# Revit family: Drain_Floor_15-Inch-Round_Zurn-Z1737_Extra-Heavy-Duty
name_source: partatom
category: Plumbing Fixtures
units: mm (PartAtom-declared; Revit-internal decimal feet)

## family parameters
Always vertical = Yes
Cut with Voids When Loaded = No
Maintain Annotation Orientation = No
OmniClass Number = 23.45.55.21
OmniClass Title = Drains (Wastes)
Part Type = Normal
Room Calculation Point = No
Round Connector Dimension = Use Radius
Shared = No
Work Plane-Based = No

## types (2) — shared parameters
Approx. Weight (Lbs) = 85 "
Assembly Code = D2030300
Body HT Dim 'E' = 5.5 "
CW Connection = No
Default Elevation = 10 "
Description = 15 INCH DIAMETER FLOOR DRAIN
Grate Open Area (Sq. In.) = 55 "
HW Connection = No
Manufacturer = Zurn Water, LLC
Manufacurer Brand = Zurn
Modified Date = 11/14/25
Pipe Size 'A' (Inner Diameter) = 7.981 "
Pipe Size 'A' (Inner Radius) = 3.991 "
Pipe Size 'A' (Nominal Diameter) = 8 "
Pipe Size 'A' (Nominal Radius) = 4 "
Pipe Size 'A' (Outer Diameter) = 8.625 "
Pipe Size 'A' (Outer Radius) = 4.313 "
Product Documentation Link = https://files.zurn.com
Product Page URL = https://www.zurn.com
Product data url = https://www.bimobject.com
URL = www.zurn.com
Vent Connection = No
Waste Connection = Yes
zero-valued in all types: CWFU, HWFU, WFU

## per-type parameters (varying)
| type | Main Material | Model | Type Comments |
| Z1737-8IP | Steel - Zurn - Stainless - Type - 304 | Z1737 | Z1737 - 8 Inch IP Threaded Outlet |
| ZM1737-8IP | Steel - Zurn- Stainless - Type - 316 | ZM1737 | ZM1737 - 8 Inch IP Threaded Outlet |

## geometry (parser evidence)
native form markers: Sweep x5
no freeform markers — native parametric forms only
